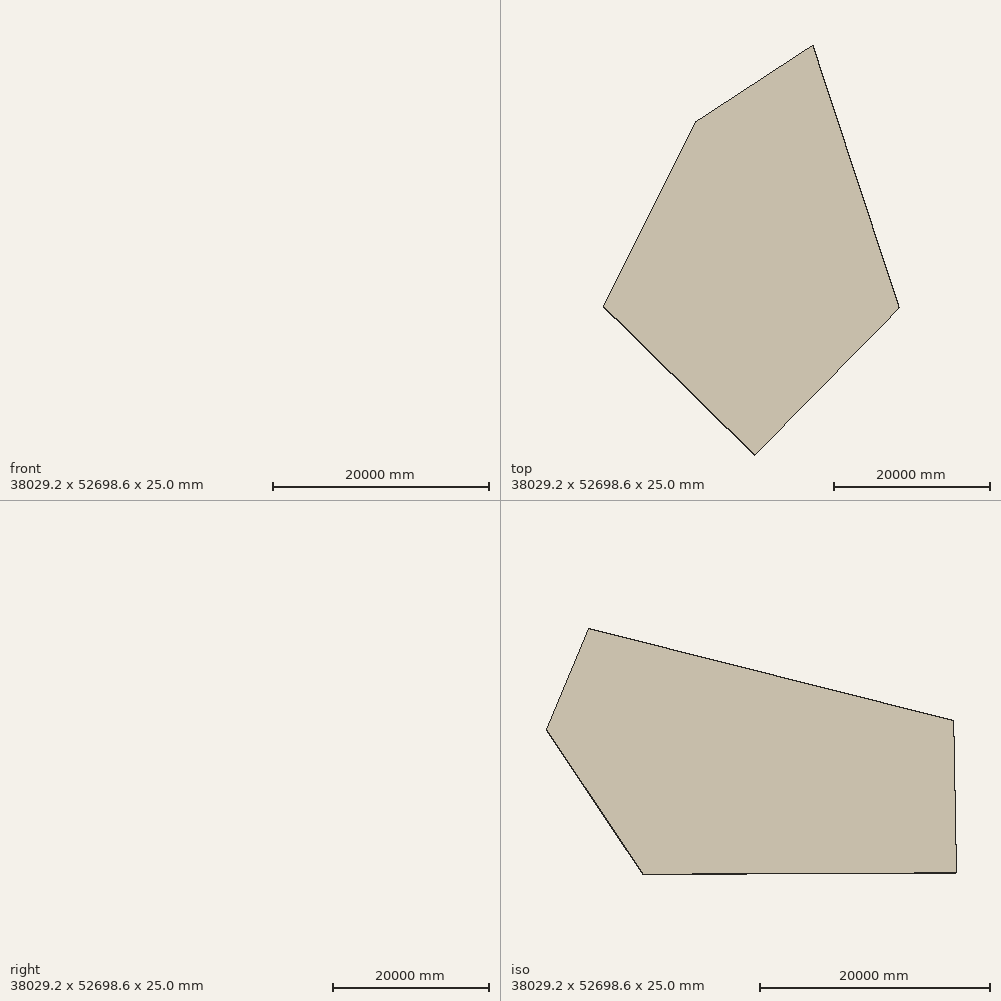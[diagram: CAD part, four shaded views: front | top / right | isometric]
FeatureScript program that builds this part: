
annotation { "Feature Type Name" : "Feature", "Feature Type Description" : "" }
export const myFeature = defineFeature(function(context is Context, id is Id, definition is map)
    precondition{}
    {
        {
            var Q0;
            Q0=qCreatedBy(makeId("Top.planeOp"),FACE);
            var sketch = newSketch(context, id + "F0", { "sketchPlane" : qUnion([Q0])});
            skLineSegment(sketch, "E0", {"start": v(19023.65, -44348.02) * mm, "end": v(30842.6, -20640.6) * mm});
            skLineSegment(sketch, "E1", {"start": v(30842.6, -20640.6) * mm, "end": v(45929.14, -10768.3) * mm});
            skLineSegment(sketch, "E2", {"start": v(45929.14, -10768.3) * mm, "end": v(57052.86, -44556.6) * mm});
            skLineSegment(sketch, "E3", {"start": v(57052.86, -44556.6) * mm, "end": v(38490.15, -63466.91) * mm});
            skLineSegment(sketch, "E4", {"start": v(38490.15, -63466.91) * mm, "end": v(19023.65, -44348.02) * mm});
            skSolve(sketch);
        }
        {
            var Q0;
            Q0=makeQuery(id+"F0.imprint","IMPRINT",FACE,{"disambiguationData":[TD([[makeQuery(id+"F0.imprint","IMPRINT",EDGE,{"derivedFrom":sQuery(id+"F0.wireOp",EDGE,"E0")}),-1.0]])]});
            extrude(context, id + "F1", {"entities" : qUnion([Q0]), "depth" : 25 * mm});
        }
    });
